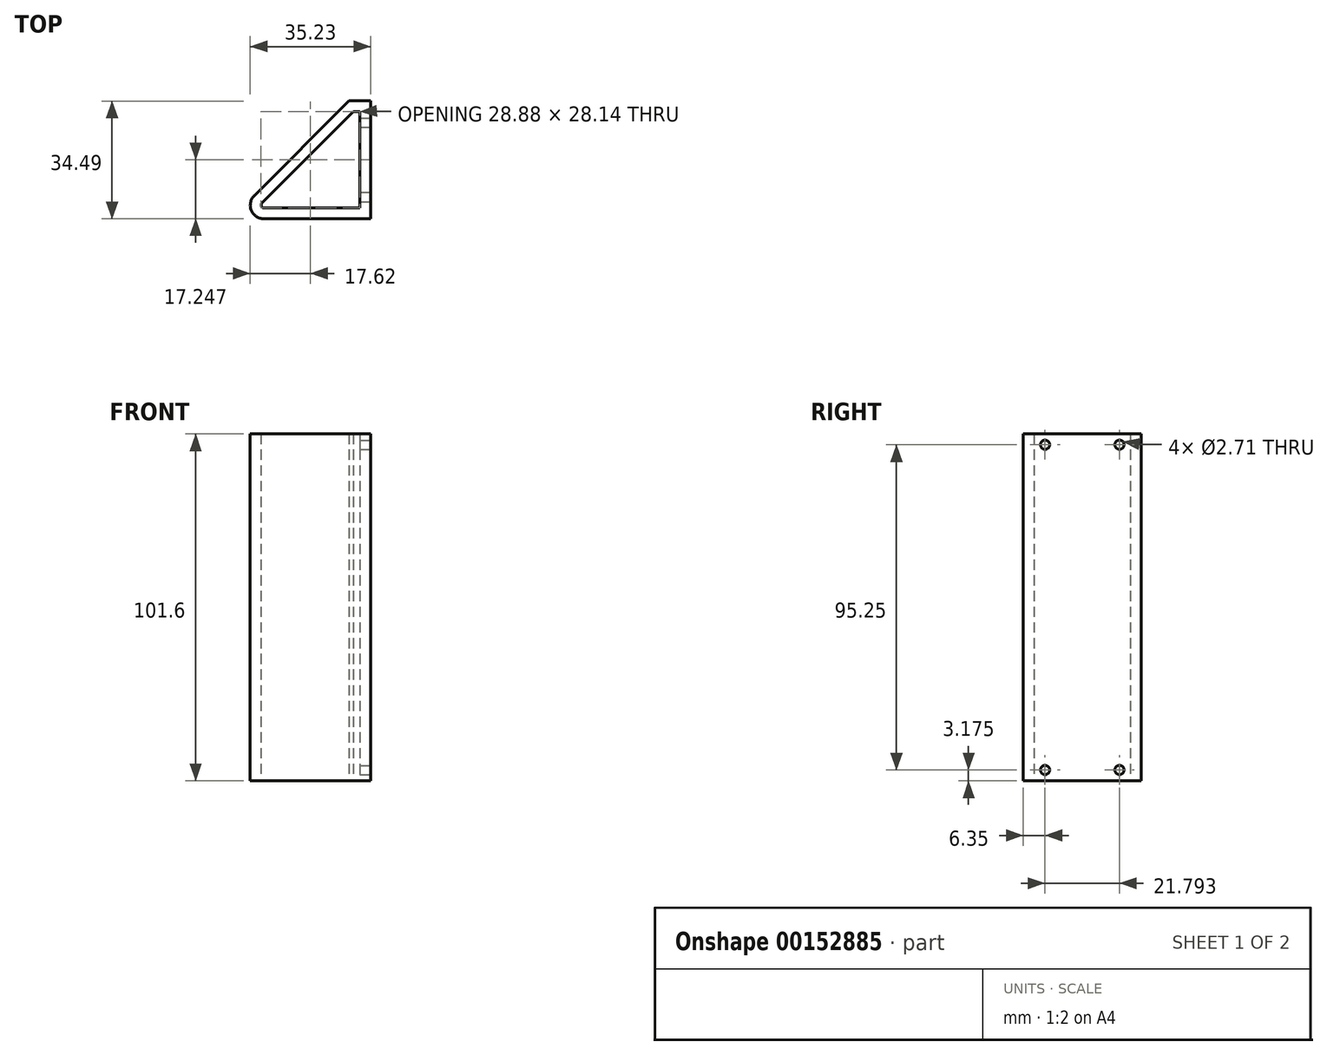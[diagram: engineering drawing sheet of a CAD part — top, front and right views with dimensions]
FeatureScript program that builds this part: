
annotation { "Feature Type Name" : "Feature", "Feature Type Description" : "" }
export const myFeature = defineFeature(function(context is Context, id is Id, definition is map)
    precondition{}
    {
        {
            var Q0;
            Q0=qCreatedBy(makeId("Top.planeOp"),FACE);
            var sketch = newSketch(context, id + "F0", { "sketchPlane" : qUnion([Q0])});
            skLineSegment(sketch, "E0", {"start": v(0.56, -1.36) * mm, "end": v(28.65, -1.36) * mm});
            skLineSegment(sketch, "E1", {"start": v(26.79, 26.79) * mm, "end": v(0, 0) * mm});
            skArc(sketch, "E2", {"start": v(-2.25, 2.25) * mm, "mid": v(-3.1, -2.08) * mm, "end": v(0.56, -4.53) * mm});
            skLineSegment(sketch, "E3", {"start": v(-2.25, 2.25) * mm, "end": v(25.47, 29.96) * mm});
            skLineSegment(sketch, "E4", {"start": v(0.56, -4.53) * mm, "end": v(31.82, -4.53) * mm});
            skLineSegment(sketch, "E5", {"start": v(31.82, -4.53) * mm, "end": v(31.82, 29.96) * mm});
            skLineSegment(sketch, "E6", {"start": v(28.65, -1.36) * mm, "end": v(28.65, -4.53) * mm, "construction": true});
            skLineSegment(sketch, "E7", {"start": v(28.65, -1.36) * mm, "end": v(31.82, -1.36) * mm, "construction": true});
            skArc(sketch, "E8", {"start": v(0, 0) * mm, "mid": v(-0.17, -0.87) * mm, "end": v(0.56, -1.36) * mm});
            skLineSegment(sketch, "E9", {"start": v(25.47, 29.96) * mm, "end": v(31.82, 29.96) * mm});
            skLineSegment(sketch, "E10", {"start": v(26.79, 26.79) * mm, "end": v(28.65, 26.79) * mm});
            skLineSegment(sketch, "E11", {"start": v(28.65, -1.36) * mm, "end": v(28.65, 26.79) * mm});
            skLineSegment(sketch, "E12", {"start": v(28.65, 26.79) * mm, "end": v(28.65, 29.96) * mm, "construction": true});
            skSolve(sketch);
        }
        {
            var Q0;
            Q0=qSketchRegion(id+"F0",true);
            extrude(context, id + "F1", {"entities" : qUnion([Q0]), "depth" : 101.6 * mm});
        }
        {
            var Q0;
            Q0=makeQuery(id+"F1.opExtrude","SWEPT_FACE",FACE,{"disambiguationData":[OSD([sQuery(id+"F0.wireOp",EDGE,"E5")])]});
            var sketch = newSketch(context, id + "F2", { "sketchPlane" : qUnion([Q0])});
            skLineSegment(sketch, "E13.bottom", {"start": v(-1.36, 0) * mm, "end": v(1.82, 0) * mm, "construction": true});
            skLineSegment(sketch, "E13.top", {"start": v(-1.36, 3.18) * mm, "end": v(1.82, 3.18) * mm, "construction": true});
            skLineSegment(sketch, "E13.left", {"start": v(-1.36, 0) * mm, "end": v(-1.36, 3.18) * mm, "construction": true});
            skLineSegment(sketch, "E13.right", {"start": v(1.82, 0) * mm, "end": v(1.82, 3.18) * mm, "construction": true});
            skLineSegment(sketch, "E14", {"start": v(29.96, 50.8) * mm, "end": v(-4.53, 50.8) * mm, "construction": true});
            skLineSegment(sketch, "E15.bottom", {"start": v(1.82, 3.18) * mm, "end": v(23.61, 3.18) * mm, "construction": true});
            skLineSegment(sketch, "E15.top", {"start": v(1.82, 98.43) * mm, "end": v(23.61, 98.43) * mm, "construction": true});
            skLineSegment(sketch, "E15.left", {"start": v(1.82, 3.17) * mm, "end": v(1.82, 98.43) * mm, "construction": true});
            skLineSegment(sketch, "E15.right", {"start": v(23.61, 3.17) * mm, "end": v(23.61, 98.43) * mm, "construction": true});
            skPoint(sketch, "E15.middle", {"position": v(12.72, 50.8) * mm});
            skCircle(sketch, "E16", {"center": v(23.61, 98.43) * mm, "radius": 1.35 * mm});
            skCircle(sketch, "E17", {"center": v(1.82, 98.43) * mm, "radius": 1.35 * mm});
            skCircle(sketch, "E18", {"center": v(1.82, 3.18) * mm, "radius": 1.35 * mm});
            skCircle(sketch, "E19", {"center": v(23.61, 3.18) * mm, "radius": 1.35 * mm});
            skSolve(sketch);
        }
        {
            var Q0;
            Q0=qSketchRegion(id+"F2",true);
            var Q1;
            Q1=makeQuery(id+"F1.opExtrude","SWEPT_FACE",FACE,{"disambiguationData":[OSD([sQuery(id+"F0.wireOp",EDGE,"E11")])]});
            extrude(context, id + "F3", {"entities" : qUnion([Q0]), "operationType" : NewBodyOperationType.REMOVE, "endBound" : BoundingType.UP_TO_SURFACE, "oppositeDirection" : true, "endBoundEntityFace" : qUnion([Q1]), "depth" : 25.4 * mm});
        }
    });
